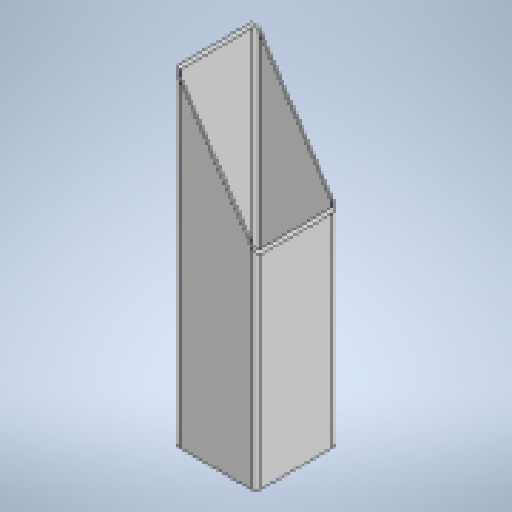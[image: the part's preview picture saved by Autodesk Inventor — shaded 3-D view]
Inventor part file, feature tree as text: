
AUTODESK INVENTOR PART (.ipt)
format: ipt  version: 2025 (Build 290162010, 162A)  size: 162,304 bytes
history: native  units: mm
features: extrude x2, sketch x2
ambient origin geometry x8: Origin, YZ Plane, XZ Plane, XY Plane, X Axis, Y Axis, Z Axis, Center Point
bodies: Solid1 (feature_tree)
feature tree (4):
  extrude  "Extrusion1"  Depth=5.0mm
  extrude  "Extrusion2"  Depth=2.0mm TaperAngle=0.0deg
  sketch  "Sketch1"  dims[d0=80.0mm d1=5.0mm]
  sketch  "Sketch2"  dims[d2=2.0mm d3=320.0mm d4=0.0mm d5=21.544344mm d6=0.0mm d7=0.0mm]
